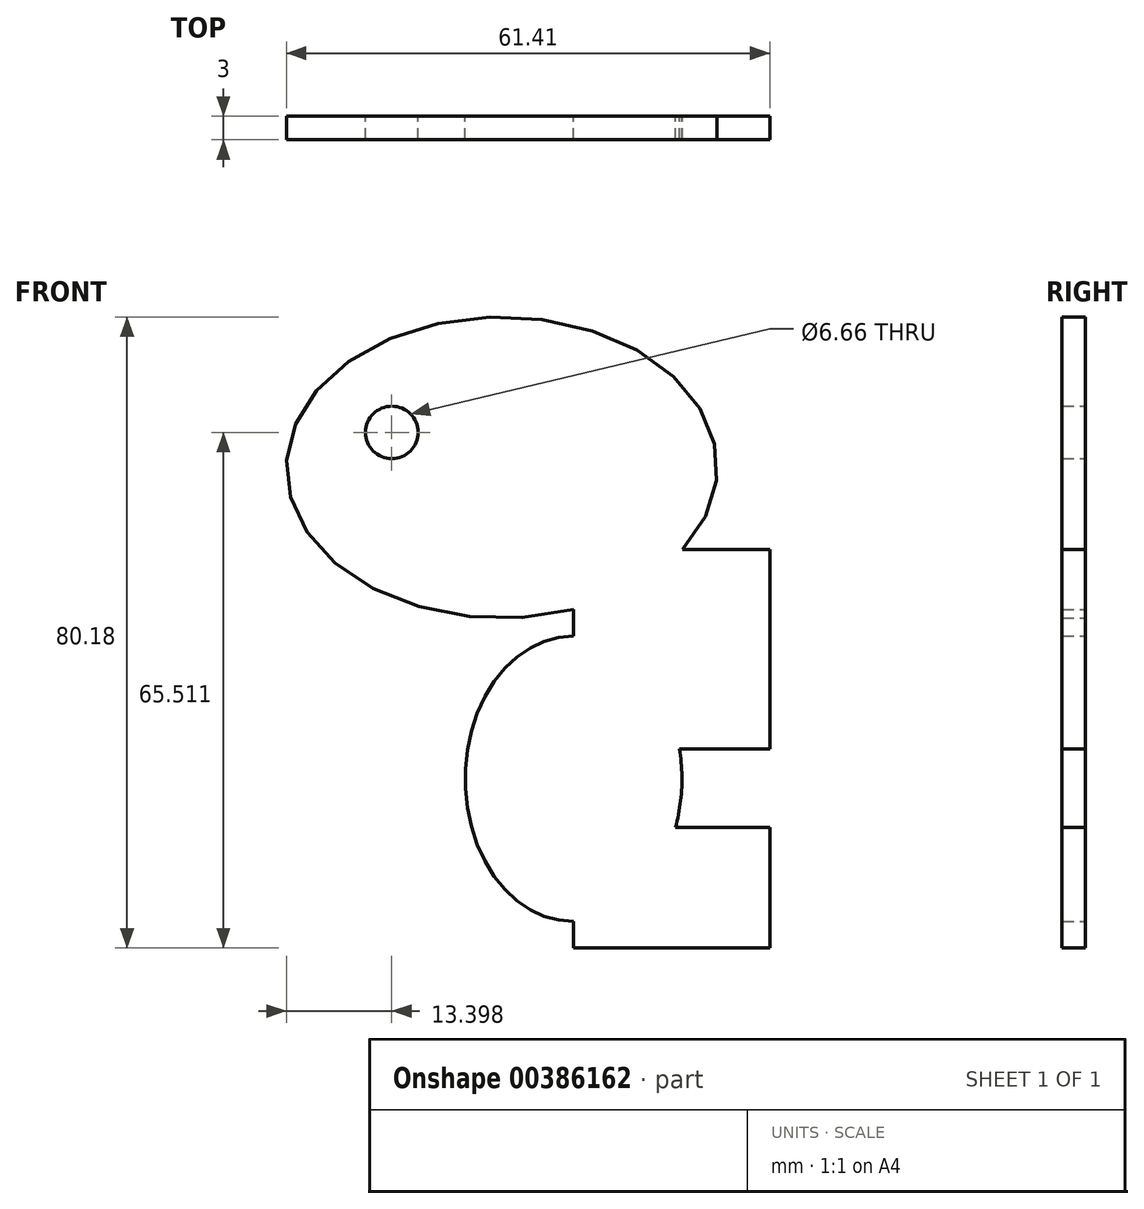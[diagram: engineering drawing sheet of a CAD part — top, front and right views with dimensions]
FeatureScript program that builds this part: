
annotation { "Feature Type Name" : "Feature", "Feature Type Description" : "" }
export const myFeature = defineFeature(function(context is Context, id is Id, definition is map)
    precondition{}
    {
        {
            var Q0;
            Q0=qCreatedBy(makeId("Front.planeOp"),FACE);
            var sketch = newSketch(context, id + "F0", { "sketchPlane" : qUnion([Q0])});
            skEllipticalArc(sketch, "E0", {});
            skLineSegment(sketch, "E1.bottom", {"start": v(22.95, 35.32) * mm, "end": v(34.05, 35.32) * mm});
            skLineSegment(sketch, "E1.top", {"start": v(9.12, -15.3) * mm, "end": v(34.05, -15.3) * mm});
            skLineSegment(sketch, "E1.left", {"start": v(9.12, 27.7) * mm, "end": v(9.12, 24.32) * mm});
            skLineSegment(sketch, "E1.right", {"start": v(34.05, 35.32) * mm, "end": v(34.05, 10.01) * mm});
            skLineSegment(sketch, "E2.bottom", {"start": v(34.05, 10.01) * mm, "end": v(21.4, 10.01) * mm});
            skLineSegment(sketch, "E2.top", {"start": v(34.05, 0) * mm, "end": v(21.4, 0) * mm});
            skLineSegment(sketch, "E3.trimOffspring", {"start": v(34.05, 0) * mm, "end": v(34.05, -15.3) * mm});
            skCircle(sketch, "E4", {"center": v(-13.96, 50.21) * mm, "radius": 3.33 * mm});
            skLineSegment(sketch, "E5", {"start": v(-21.64, 34.04) * mm, "end": v(-10.62, 34.04) * mm});
            skEllipticalArc(sketch, "E6", {});
            skLineSegment(sketch, "E7.trimOffspring", {"start": v(9.12, -11.92) * mm, "end": v(9.12, -15.3) * mm});
            skEllipticalArc(sketch, "E8.trimOffspring", {});
            const initialGuessF0  = {"E0": [0, 0.04574435204267502, -1, 0, 0.027362219989299774, 0.01913545207767404, 2.565618048042884, 1.9104257686248352], "E6": [0.009115387685596943, 0.00620107461119743, -1, 0, 0.013772157952189445, 0.018119133243126827, 4.71238898038469, 1.5707963267948966], "E8.trimOffspring": [0.009115387685596943, 0.00620107461119743, -1, 0, 0.013772157952189445, 0.018119133243126827, 2.7922938574748732, 3.3534553442698436]};
            skSetInitialGuess(sketch, initialGuessF0);
            skSolve(sketch);
        }
        {
            var Q0;
            {var subQ8=sQuery(id+"F0.wireOp",EDGE,"E1.bottom");Q0=makeQuery(id+"F0.imprint","IMPRINT",FACE,{"disambiguationData":[TD([[makeQuery(id+"F0.imprint","IMPRINT",EDGE,{"derivedFrom":subQ8}),-1.0]])]});}
            extrude(context, id + "F1", {"entities" : qUnion([Q0]), "depth" : 3 * mm});
        }
    });
